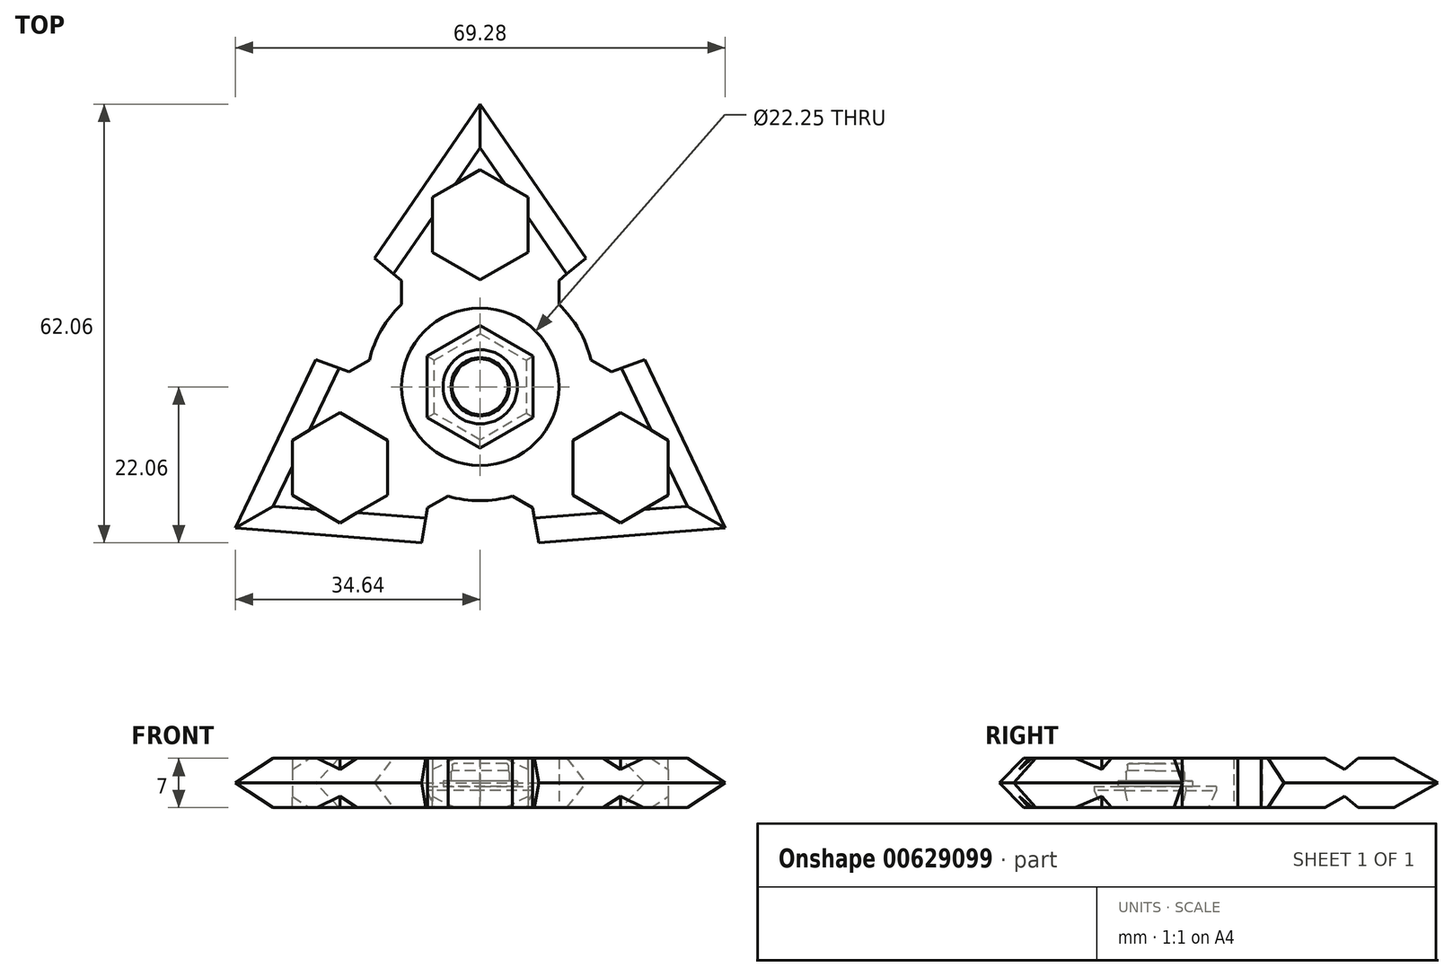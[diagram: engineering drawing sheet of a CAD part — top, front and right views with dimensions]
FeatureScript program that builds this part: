
annotation { "Feature Type Name" : "Feature", "Feature Type Description" : "" }
export const myFeature = defineFeature(function(context is Context, id is Id, definition is map)
    precondition{}
    {
        {
            var Q0;
            Q0=qCreatedBy(makeId("Top.planeOp"),FACE);
            var sketch = newSketch(context, id + "F0", { "sketchPlane" : qUnion([Q0])});
            skCircle(sketch, "E0", {"center": v(0, 0) * mm, "radius": 11.12 * mm});
            skCircle(sketch, "E1.0", {"center": v(0, 0) * mm, "radius": 16.12 * mm});
            skLineSegment(sketch, "E2", {"start": v(-11.12, 0) * mm, "end": v(-11.12, 15) * mm});
            skLineSegment(sketch, "E3", {"start": v(-11.12, 15) * mm, "end": v(-14.96, 18.21) * mm});
            skLineSegment(sketch, "E4", {"start": v(-14.96, 18.21) * mm, "end": v(0, 40) * mm});
            skLineSegment(sketch, "E5", {"start": v(0, 40) * mm, "end": v(14.96, 18.21) * mm});
            skLineSegment(sketch, "E6", {"start": v(14.96, 18.21) * mm, "end": v(11.12, 15) * mm});
            skLineSegment(sketch, "E7", {"start": v(11.12, 15) * mm, "end": v(11.12, 0) * mm});
            skLineSegment(sketch, "E8", {"start": v(11.12, 0) * mm, "end": v(-11.12, 0) * mm});
            skLineSegment(sketch, "E9.1.0", {"start": v(-34.64, -20) * mm, "end": v(-23.25, 3.84) * mm});
            skLineSegment(sketch, "E9.1.1", {"start": v(-8.3, -22.06) * mm, "end": v(-34.64, -20) * mm});
            skLineSegment(sketch, "E9.1.2", {"start": v(-7.43, -17.13) * mm, "end": v(-8.3, -22.06) * mm});
            skLineSegment(sketch, "E9.1.3", {"start": v(5.56, -9.63) * mm, "end": v(-7.43, -17.13) * mm});
            skLineSegment(sketch, "E9.1.4", {"start": v(-18.55, 2.13) * mm, "end": v(-5.56, 9.63) * mm});
            skLineSegment(sketch, "E9.1.5", {"start": v(-23.25, 3.84) * mm, "end": v(-18.55, 2.13) * mm});
            skLineSegment(sketch, "E9.2.0", {"start": v(34.64, -20) * mm, "end": v(8.3, -22.06) * mm});
            skLineSegment(sketch, "E9.2.1", {"start": v(23.25, 3.84) * mm, "end": v(34.64, -20) * mm});
            skLineSegment(sketch, "E9.2.2", {"start": v(18.55, 2.13) * mm, "end": v(23.25, 3.84) * mm});
            skLineSegment(sketch, "E9.2.3", {"start": v(5.56, 9.63) * mm, "end": v(18.55, 2.13) * mm});
            skLineSegment(sketch, "E9.2.4", {"start": v(7.43, -17.13) * mm, "end": v(-5.56, -9.63) * mm});
            skLineSegment(sketch, "E9.2.5", {"start": v(8.3, -22.06) * mm, "end": v(7.43, -17.13) * mm});
            skCircle(sketch, "E10.cCircle", {"center": v(0, 22.92) * mm, "radius": 6.75 * mm, "construction": true});
            skLineSegment(sketch, "E10.0", {"start": v(6.75, 26.82) * mm, "end": v(6.75, 19.02) * mm});
            skLineSegment(sketch, "E10.1", {"start": v(6.75, 19.02) * mm, "end": v(0, 15.12) * mm});
            skLineSegment(sketch, "E10.2", {"start": v(0, 15.12) * mm, "end": v(-6.75, 19.02) * mm});
            skLineSegment(sketch, "E10.3", {"start": v(-6.75, 19.02) * mm, "end": v(-6.75, 26.82) * mm});
            skLineSegment(sketch, "E10.4", {"start": v(-6.75, 26.82) * mm, "end": v(0, 30.71) * mm});
            skLineSegment(sketch, "E10.5", {"start": v(0, 30.71) * mm, "end": v(6.75, 26.82) * mm});
            skPoint(sketch, "E10.0.midPoint", {"position": v(6.75, 22.92) * mm});
            skLineSegment(sketch, "E11.1.0", {"start": v(-19.85, -3.67) * mm, "end": v(-13.1, -7.56) * mm});
            skLineSegment(sketch, "E11.1.1", {"start": v(-26.6, -7.56) * mm, "end": v(-19.85, -3.67) * mm});
            skLineSegment(sketch, "E11.1.2", {"start": v(-26.6, -15.36) * mm, "end": v(-26.6, -7.56) * mm});
            skLineSegment(sketch, "E11.1.3", {"start": v(-19.85, -19.25) * mm, "end": v(-26.6, -15.36) * mm});
            skLineSegment(sketch, "E11.1.4", {"start": v(-13.1, -15.36) * mm, "end": v(-19.85, -19.25) * mm});
            skLineSegment(sketch, "E11.1.5", {"start": v(-13.1, -7.56) * mm, "end": v(-13.1, -15.36) * mm});
            skLineSegment(sketch, "E11.2.0", {"start": v(13.1, -15.36) * mm, "end": v(13.1, -7.56) * mm});
            skLineSegment(sketch, "E11.2.1", {"start": v(19.85, -19.25) * mm, "end": v(13.1, -15.36) * mm});
            skLineSegment(sketch, "E11.2.2", {"start": v(26.6, -15.36) * mm, "end": v(19.85, -19.25) * mm});
            skLineSegment(sketch, "E11.2.3", {"start": v(26.6, -7.56) * mm, "end": v(26.6, -15.36) * mm});
            skLineSegment(sketch, "E11.2.4", {"start": v(19.85, -3.67) * mm, "end": v(26.6, -7.56) * mm});
            skLineSegment(sketch, "E11.2.5", {"start": v(13.1, -7.56) * mm, "end": v(19.85, -3.67) * mm});
            skSolve(sketch);
        }
        {
            var Q0;
            Q0=makeQuery(id+"F0.imprint","IMPRINT",FACE,{"disambiguationData":[TD([[makeQuery(id+"F0.imprint","IMPRINT",EDGE,{"derivedFrom":sQuery(id+"F0.wireOp",EDGE,"E9.2.0")}),-1.0]])]});
            var Q1;
            {var subQ5=sQuery(id+"F0.wireOp",EDGE,"E9.2.3");var subQ6=sQuery(id+"F0.wireOp",EDGE,"E1.0");var subQ7=makeQuery(id+"F0.imprint","INTERSECT",VERTEX,{"derivedFrom":[subQ6,subQ5]});Q1=makeQuery(id+"F0.imprint","IMPRINT",FACE,{"disambiguationData":[TD([[makeQuery(id+"F0.imprint","IMPRINT",EDGE,{"disambiguationData":[TD([[subQ7,1.0]])],"derivedFrom":subQ6}),1.0]])]});}
            var Q2;
            {var subQ0=sQuery(id+"F0.wireOp",EDGE,"E9.1.3");var subQ1=sQuery(id+"F0.wireOp",EDGE,"E1.0");var subQ2=makeQuery(id+"F0.imprint","INTERSECT",VERTEX,{"derivedFrom":[subQ1,subQ0]});Q2=makeQuery(id+"F0.imprint","IMPRINT",FACE,{"disambiguationData":[TD([[makeQuery(id+"F0.imprint","IMPRINT",EDGE,{"disambiguationData":[TD([[subQ2,-1.0]])],"derivedFrom":subQ1}),1.0]])]});}
            var Q3;
            {var subQ0=sQuery(id+"F0.wireOp",EDGE,"E9.1.3");var subQ1=sQuery(id+"F0.wireOp",EDGE,"E0");var subQ2=makeQuery(id+"F0.imprint","INTERSECT",VERTEX,{"derivedFrom":[subQ1,subQ0]});Q3=makeQuery(id+"F0.imprint","IMPRINT",FACE,{"disambiguationData":[TD([[makeQuery(id+"F0.imprint","IMPRINT",EDGE,{"disambiguationData":[TD([[subQ2,1.0]])],"derivedFrom":subQ1}),-1.0]])]});}
            var Q4;
            {var subQ1=sQuery(id+"F0.wireOp",EDGE,"E1.0");var subQ8=sQuery(id+"F0.wireOp",EDGE,"E9.1.4");var subQ10=makeQuery(id+"F0.imprint","INTERSECT",VERTEX,{"derivedFrom":[subQ1,subQ8]});Q4=makeQuery(id+"F0.imprint","IMPRINT",FACE,{"disambiguationData":[TD([[makeQuery(id+"F0.imprint","IMPRINT",EDGE,{"disambiguationData":[TD([[subQ10,-1.0]])],"derivedFrom":subQ1}),1.0]])]});}
            var Q5;
            {var subQ0=sQuery(id+"F0.wireOp",EDGE,"E2");var subQ1=sQuery(id+"F0.wireOp",EDGE,"E1.0");var subQ2=makeQuery(id+"F0.imprint","INTERSECT",VERTEX,{"derivedFrom":[subQ1,subQ0]});Q5=makeQuery(id+"F0.imprint","IMPRINT",FACE,{"disambiguationData":[TD([[makeQuery(id+"F0.imprint","IMPRINT",EDGE,{"disambiguationData":[TD([[subQ2,-1.0]])],"derivedFrom":subQ1}),1.0]])]});}
            var Q6;
            {var subQ1=sQuery(id+"F0.wireOp",EDGE,"E0");var subQ3=sQuery(id+"F0.wireOp",EDGE,"E9.1.4");var subQ4=makeQuery(id+"F0.imprint","INTERSECT",VERTEX,{"derivedFrom":[subQ1,subQ3]});Q6=makeQuery(id+"F0.imprint","IMPRINT",FACE,{"disambiguationData":[TD([[makeQuery(id+"F0.imprint","IMPRINT",EDGE,{"disambiguationData":[TD([[subQ4,1.0]])],"derivedFrom":subQ3}),-1.0]])]});}
            var Q7;
            {var subQ5=sQuery(id+"F0.wireOp",EDGE,"E9.1.4");var subQ6=sQuery(id+"F0.wireOp",EDGE,"E0");var subQ7=makeQuery(id+"F0.imprint","INTERSECT",VERTEX,{"derivedFrom":[subQ6,subQ5]});Q7=makeQuery(id+"F0.imprint","IMPRINT",FACE,{"disambiguationData":[TD([[makeQuery(id+"F0.imprint","IMPRINT",EDGE,{"disambiguationData":[TD([[subQ7,1.0]])],"derivedFrom":subQ6}),-1.0]])]});}
            var Q8;
            {var subQ1=sQuery(id+"F0.wireOp",EDGE,"E0");var subQ3=sQuery(id+"F0.wireOp",EDGE,"E9.2.3");var subQ4=makeQuery(id+"F0.imprint","INTERSECT",VERTEX,{"derivedFrom":[subQ1,subQ3]});Q8=makeQuery(id+"F0.imprint","IMPRINT",FACE,{"disambiguationData":[TD([[makeQuery(id+"F0.imprint","IMPRINT",EDGE,{"disambiguationData":[TD([[subQ4,-1.0]])],"derivedFrom":subQ3}),-1.0]])]});}
            var Q9;
            {var subQ0=sQuery(id+"F0.wireOp",EDGE,"E7");var subQ1=sQuery(id+"F0.wireOp",EDGE,"E1.0");var subQ2=makeQuery(id+"F0.imprint","INTERSECT",VERTEX,{"derivedFrom":[subQ1,subQ0]});Q9=makeQuery(id+"F0.imprint","IMPRINT",FACE,{"disambiguationData":[TD([[makeQuery(id+"F0.imprint","IMPRINT",EDGE,{"disambiguationData":[TD([[subQ2,1.0]])],"derivedFrom":subQ1}),1.0]])]});}
            var Q10;
            {var subQ0=sQuery(id+"F0.wireOp",EDGE,"E3");Q10=makeQuery(id+"F0.imprint","IMPRINT",FACE,{"disambiguationData":[TD([[makeQuery(id+"F0.imprint","IMPRINT",EDGE,{"derivedFrom":subQ0}),-1.0]])]});}
            var Q11;
            Q11=makeQuery(id+"F0.imprint","IMPRINT",FACE,{"disambiguationData":[TD([[makeQuery(id+"F0.imprint","IMPRINT",EDGE,{"derivedFrom":sQuery(id+"F0.wireOp",EDGE,"E9.1.0")}),-1.0]])]});
            extrude(context, id + "F1", {"entities" : qUnion([Q0, Q1, Q2, Q3, Q4, Q5, Q6, Q7, Q8, Q9, Q10, Q11]), "depth" : 7 * mm, "offsetDistance" : 25 * mm});
        }
        {
            var Q0;
            Q0=makeQuery(id+"F1.opExtrude","CAP_EDGE",EDGE,{"disambiguationData":[OSD([sQuery(id+"F0.wireOp",EDGE,"E9.1.1")])],"isStart":true});
            var Q1;
            Q1=makeQuery(id+"F1.opExtrude","CAP_EDGE",EDGE,{"disambiguationData":[OSD([sQuery(id+"F0.wireOp",EDGE,"E9.1.0")])],"isStart":true});
            var Q2;
            Q2=makeQuery(id+"F1.opExtrude","CAP_EDGE",EDGE,{"disambiguationData":[OSD([sQuery(id+"F0.wireOp",EDGE,"E9.1.0")])],"isStart":false});
            var Q3;
            Q3=makeQuery(id+"F1.opExtrude","CAP_EDGE",EDGE,{"disambiguationData":[OSD([sQuery(id+"F0.wireOp",EDGE,"E9.1.1")])],"isStart":false});
            var Q4;
            Q4=makeQuery(id+"F1.opExtrude","CAP_EDGE",EDGE,{"disambiguationData":[OSD([sQuery(id+"F0.wireOp",EDGE,"E9.2.0")])],"isStart":false});
            var Q5;
            Q5=makeQuery(id+"F1.opExtrude","CAP_EDGE",EDGE,{"disambiguationData":[OSD([sQuery(id+"F0.wireOp",EDGE,"E9.2.0")])],"isStart":true});
            var Q6;
            Q6=makeQuery(id+"F1.opExtrude","CAP_EDGE",EDGE,{"disambiguationData":[OSD([sQuery(id+"F0.wireOp",EDGE,"E9.2.1")])],"isStart":false});
            var Q7;
            Q7=makeQuery(id+"F1.opExtrude","CAP_EDGE",EDGE,{"disambiguationData":[OSD([sQuery(id+"F0.wireOp",EDGE,"E9.2.1")])],"isStart":true});
            var Q8;
            Q8=makeQuery(id+"F1.opExtrude","CAP_EDGE",EDGE,{"disambiguationData":[OSD([sQuery(id+"F0.wireOp",EDGE,"E5")])],"isStart":false});
            var Q9;
            Q9=makeQuery(id+"F1.opExtrude","CAP_EDGE",EDGE,{"disambiguationData":[OSD([sQuery(id+"F0.wireOp",EDGE,"E5")])],"isStart":true});
            var Q10;
            Q10=makeQuery(id+"F1.opExtrude","CAP_EDGE",EDGE,{"disambiguationData":[OSD([sQuery(id+"F0.wireOp",EDGE,"E4")])],"isStart":false});
            var Q11;
            Q11=makeQuery(id+"F1.opExtrude","CAP_EDGE",EDGE,{"disambiguationData":[OSD([sQuery(id+"F0.wireOp",EDGE,"E4")])],"isStart":true});
            chamfer(context, id + "F2", {"entities" : qUnion([Q0, Q1, Q2, Q3, Q4, Q5, Q6, Q7, Q8, Q9, Q10, Q11]), "chamferType" : ChamferType.OFFSET_ANGLE, "width" : 3.5 * mm, "oppositeDirection" : false, "angle" : 45 * degree, "tangentPropagation" : true});
        }
        {
            var Q0;
            Q0=qCreatedBy(makeId("Top.planeOp"),FACE);
            var sketch = newSketch(context, id + "F3", { "sketchPlane" : qUnion([Q0])});
            skCircle(sketch, "E12", {"center": v(0, 0) * mm, "radius": 7.5 * mm});
            skSolve(sketch);
        }
        {
            var Q0;
            Q0 = qSketchRegion(id + "F3", true);
            extrude(context, id + "F4", {"entities" : qUnion([Q0]), "depth" : 2 * mm, "offsetDistance" : 25 * mm});
        }
        {
            var Q0;
            Q0=makeQuery(id+"F4.opExtrude","CAP_FACE",FACE,{"disambiguationData":[OSD([sQuery(id+"F3.wireOp",EDGE,"E12")])],"isStart":false});
            var sketch = newSketch(context, id + "F5", { "sketchPlane" : qUnion([Q0])});
            skCircle(sketch, "E13", {"center": v(0, 0) * mm, "radius": 5.25 * mm});
            skSolve(sketch);
        }
        {
            var Q0;
            Q0 = qSketchRegion(id + "F5", true);
            extrude(context, id + "F6", {"entities" : qUnion([Q0]), "operationType" : NewBodyOperationType.ADD, "depth" : .75 * mm, "offsetDistance" : 25 * mm});
        }
        {
            var Q0;
            Q0=makeQuery(id+"F6.opExtrude","CAP_FACE",FACE,{"disambiguationData":[OSD([sQuery(id+"F5.wireOp",EDGE,"E13")])],"isStart":false});
            var sketch = newSketch(context, id + "F7", { "sketchPlane" : qUnion([Q0])});
            skCircle(sketch, "E14", {"center": v(0, 0) * mm, "radius": 4.12 * mm});
            skSolve(sketch);
        }
        {
            var Q0;
            Q0 = qSketchRegion(id + "F7", true);
            extrude(context, id + "F8", {"entities" : qUnion([Q0]), "operationType" : NewBodyOperationType.ADD, "depth" : 2.5 * mm, "offsetDistance" : 25 * mm});
        }
        {
            var Q0;
            Q0=makeQuery(id+"F8.opExtrude","CAP_EDGE",EDGE,{"disambiguationData":[OSD([sQuery(id+"F7.wireOp",EDGE,"E14")])],"isStart":false});
            fillet(context, id + "F9", {"entities" : qUnion([Q0]), "radius" : 0.25 * mm, "tangentPropagation" : true, "allowEdgeOverflow" : false});
        }
        {
            var Q0;
            Q0=makeQuery(id+"F4.opExtrude","CAP_EDGE",EDGE,{"disambiguationData":[OSD([sQuery(id+"F3.wireOp",EDGE,"E12")])],"isStart":true});
            chamfer(context, id + "F10", {"entities" : qUnion([Q0]), "chamferType" : ChamferType.OFFSET_ANGLE, "width" : 1 * mm, "oppositeDirection" : false, "angle" : 22.5 * degree, "tangentPropagation" : true});
        }
        {
            var Q0;
            Q0=qCreatedBy(makeId("Top.planeOp"),FACE);
            var sketch = newSketch(context, id + "F11", { "sketchPlane" : qUnion([Q0])});
            skCircle(sketch, "E15.cCircle", {"center": v(0, 0) * mm, "radius": 7.5 * mm, "construction": true});
            skLineSegment(sketch, "E15.0", {"start": v(7.5, 4.33) * mm, "end": v(7.5, -4.33) * mm});
            skLineSegment(sketch, "E15.1", {"start": v(7.5, -4.33) * mm, "end": v(0, -8.66) * mm});
            skLineSegment(sketch, "E15.2", {"start": v(0, -8.66) * mm, "end": v(-7.5, -4.33) * mm});
            skLineSegment(sketch, "E15.3", {"start": v(-7.5, -4.33) * mm, "end": v(-7.5, 4.33) * mm});
            skLineSegment(sketch, "E15.4", {"start": v(-7.5, 4.33) * mm, "end": v(0, 8.66) * mm});
            skLineSegment(sketch, "E15.5", {"start": v(0, 8.66) * mm, "end": v(7.5, 4.33) * mm});
            skPoint(sketch, "E15.0.midPoint", {"position": v(7.5, 0) * mm});
            skSolve(sketch);
        }
        {
            var Q0;
            Q0 = qSketchRegion(id + "F11", true);
            extrude(context, id + "F12", {"entities" : qUnion([Q0]), "depth" : 3 * mm, "offsetDistance" : 25 * mm});
        }
        {
            var Q0;
            Q0=makeQuery(id+"F12.opExtrude","CAP_FACE",FACE,{"disambiguationData":[OSD([sQuery(id+"F11.wireOp",EDGE,"E15.0"),sQuery(id+"F11.wireOp",EDGE,"E15.1"),sQuery(id+"F11.wireOp",EDGE,"E15.2"),sQuery(id+"F11.wireOp",EDGE,"E15.3"),sQuery(id+"F11.wireOp",EDGE,"E15.4"),sQuery(id+"F11.wireOp",EDGE,"E15.5")])],"isStart":false});
            var sketch = newSketch(context, id + "F13", { "sketchPlane" : qUnion([Q0])});
            skCircle(sketch, "E16", {"center": v(0, 0) * mm, "radius": 5.25 * mm});
            skSolve(sketch);
        }
        {
            var Q0;
            Q0 = qSketchRegion(id + "F13", true);
            extrude(context, id + "F14", {"entities" : qUnion([Q0]), "operationType" : NewBodyOperationType.ADD, "depth" : 0.75 * mm, "offsetDistance" : 25 * mm});
        }
        {
            var Q0;
            Q0=makeQuery(id+"F14.opExtrude","CAP_FACE",FACE,{"disambiguationData":[OSD([sQuery(id+"F13.wireOp",EDGE,"E16")])],"isStart":false});
            var sketch = newSketch(context, id + "F15", { "sketchPlane" : qUnion([Q0])});
            skCircle(sketch, "E17", {"center": v(0, 0) * mm, "radius": 3.95 * mm});
            skSolve(sketch);
        }
        {
            var Q0;
            Q0 = qSketchRegion(id + "F15", true);
            extrude(context, id + "F16", {"entities" : qUnion([Q0]), "operationType" : NewBodyOperationType.ADD, "depth" : 2.5 * mm, "offsetDistance" : 25 * mm});
        }
        {
            var Q0;
            Q0=makeQuery(id+"F16.opExtrude","CAP_FACE",FACE,{"disambiguationData":[OSD([sQuery(id+"F15.wireOp",EDGE,"E17")])],"isStart":false});
            fillet(context, id + "F17", {"entities" : qUnion([Q0]), "radius" : 0.25 * mm, "tangentPropagation" : true, "allowEdgeOverflow" : false});
        }
        {
            var Q0;
            Q0=makeQuery(id+"F12.opExtrude","CAP_FACE",FACE,{"disambiguationData":[OSD([sQuery(id+"F11.wireOp",EDGE,"E15.0"),sQuery(id+"F11.wireOp",EDGE,"E15.1"),sQuery(id+"F11.wireOp",EDGE,"E15.2"),sQuery(id+"F11.wireOp",EDGE,"E15.3"),sQuery(id+"F11.wireOp",EDGE,"E15.4"),sQuery(id+"F11.wireOp",EDGE,"E15.5")])],"isStart":true});
            chamfer(context, id + "F18", {"entities" : qUnion([Q0]), "chamferType" : ChamferType.OFFSET_ANGLE, "width" : 1 * mm, "oppositeDirection" : false, "angle" : 67.5 * degree, "tangentPropagation" : true});
        }
    });
